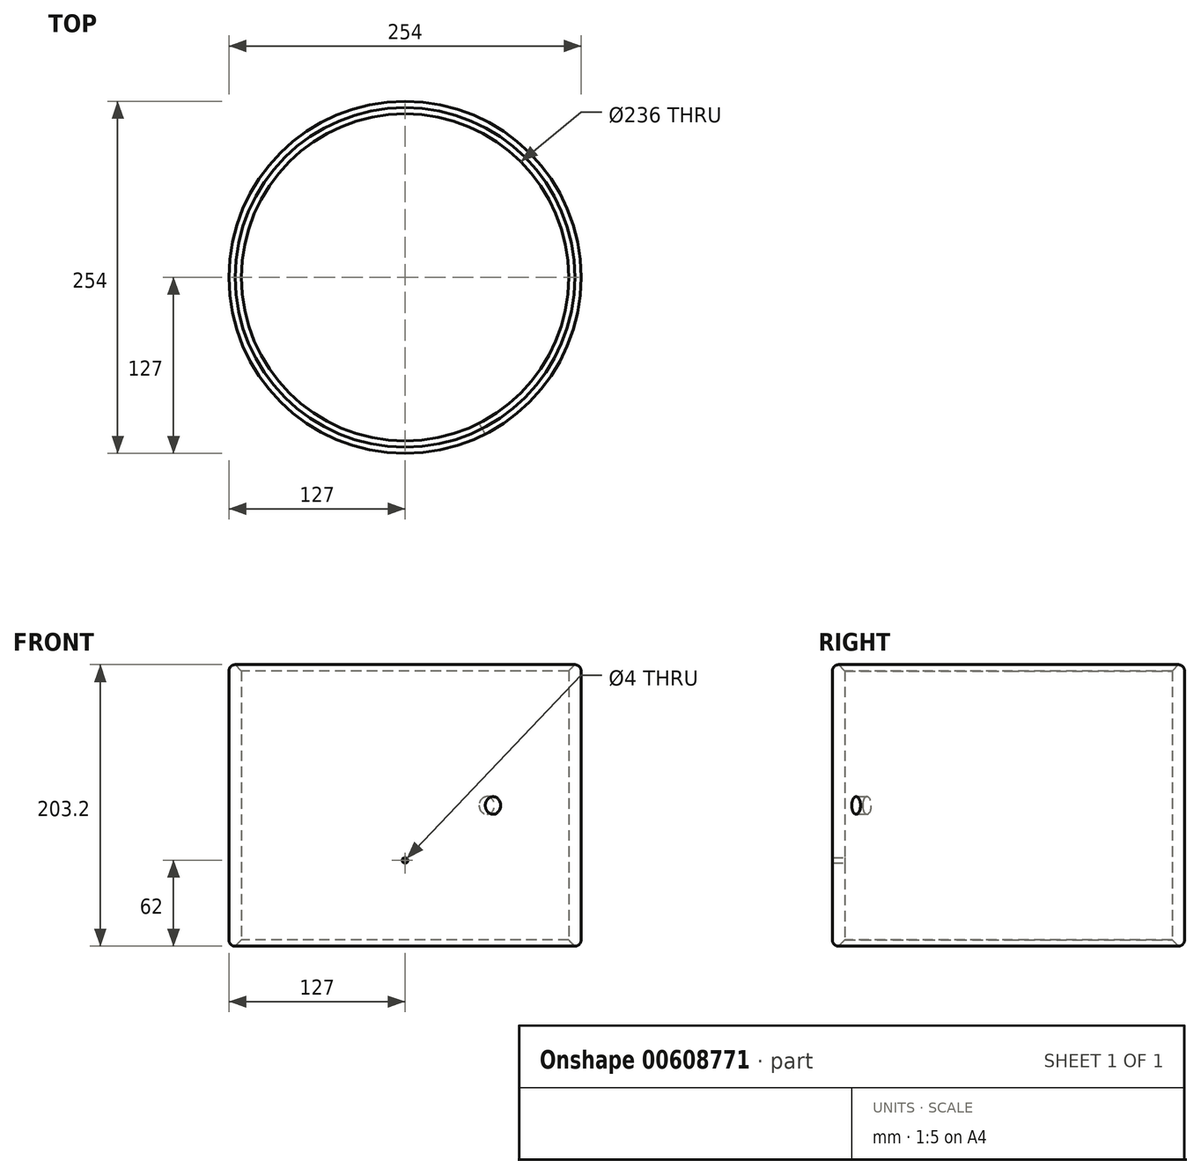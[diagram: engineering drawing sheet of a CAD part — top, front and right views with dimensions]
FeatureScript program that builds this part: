
annotation { "Feature Type Name" : "Feature", "Feature Type Description" : "" }
export const myFeature = defineFeature(function(context is Context, id is Id, definition is map)
    precondition{}
    {
        {
            var Q0;
            Q0=qCreatedBy(makeId("Top.planeOp"),FACE);
            var sketch = newSketch(context, id + "F0", { "sketchPlane" : qUnion([Q0])});
            skCircle(sketch, "E0", {"center": v(0, 0) * mm, "radius": 127 * mm});
            skCircle(sketch, "E1.0", {"center": v(0, 0) * mm, "radius": 118 * mm});
            skCircle(sketch, "E2.0", {"center": v(0, 0) * mm, "radius": 122.5 * mm});
            skLineSegment(sketch, "E3", {"start": v(0, 0) * mm, "end": v(0, 54.17) * mm, "construction": true});
            skSolve(sketch);
        }
        {
            var Q0;
            Q0=makeQuery(id+"F0.imprint","IMPRINT",FACE,{"disambiguationData":[TD([[makeQuery(id+"F0.imprint","IMPRINT",EDGE,{"derivedFrom":sQuery(id+"F0.wireOp",EDGE,"E0")}),1.0]])]});
            var Q1;
            Q1=makeQuery(id+"F0.imprint","IMPRINT",FACE,{"disambiguationData":[TD([[makeQuery(id+"F0.imprint","IMPRINT",EDGE,{"derivedFrom":sQuery(id+"F0.wireOp",EDGE,"E1.0")}),-1.0]])]});
            extrude(context, id + "F1", {"entities" : qUnion([Q0, Q1]), "depth" : 203.2 * mm, "offsetDistance" : 25 * mm});
        }
        {
            var Q0;
            Q0=makeQuery(id+"F1.opExtrude","CAP_EDGE",EDGE,{"disambiguationData":[OSD([sQuery(id+"F0.wireOp",EDGE,"E1.0")])],"isStart":false});
            chamfer(context, id + "F2", {"entities" : qUnion([Q0]), "width" : 4.5 * mm, "tangentPropagation" : true});
        }
        {
            var Q0;
            Q0=makeQuery(id+"F1.opExtrude","CAP_EDGE",EDGE,{"disambiguationData":[OSD([sQuery(id+"F0.wireOp",EDGE,"E0")])],"isStart":false});
            fillet(context, id + "F3", {"entities" : qUnion([Q0]), "radius" : 4.5 * mm, "tangentPropagation" : true, "allowEdgeOverflow" : false});
        }
        {
            var Q0;
            Q0=makeQuery(id+"F1.opExtrude","CAP_EDGE",EDGE,{"disambiguationData":[OSD([sQuery(id+"F0.wireOp",EDGE,"E1.0")])],"isStart":true});
            chamfer(context, id + "F4", {"entities" : qUnion([Q0]), "width" : 4.5 * mm, "tangentPropagation" : true});
        }
        {
            var Q0;
            Q0=makeQuery(id+"F1.opExtrude","CAP_EDGE",EDGE,{"disambiguationData":[OSD([sQuery(id+"F0.wireOp",EDGE,"E0")])],"isStart":true});
            fillet(context, id + "F5", {"entities" : qUnion([Q0]), "radius" : 4.5 * mm, "tangentPropagation" : true, "allowEdgeOverflow" : false});
        }
        {
            var Q0;
            Q0=sQuery(id+"F0.wireOp",EDGE,"E3");
            var Q1;
            Q1=sQuery(id+"F0.wireOp",VERTEX,"E3.start");
            cPlane(context, id + "F6", {"entities" : qUnion([Q0, Q1]), "cplaneType" : CPlaneType.LINE_POINT, "offset" : 25 * mm, "width" : 150 * mm, "height" : 150 * mm});
        }
        {
            var Q0;
            Q0=qCreatedBy(id+"F6.planeOp",FACE);
            var sketch = newSketch(context, id + "F7", { "sketchPlane" : qUnion([Q0])});
            skCircle(sketch, "E4", {"center": v(0, 101.6) * mm, "radius": 2 * mm});
            skLineSegment(sketch, "E5", {"start": v(0, 0) * mm, "end": v(0, 62) * mm, "construction": true});
            skCircle(sketch, "E6", {"center": v(0, 62) * mm, "radius": 2 * mm});
            skLineSegment(sketch, "E7", {"start": v(0, 101.6) * mm, "end": v(-27.1, 101.6) * mm, "construction": true});
            skCircle(sketch, "E8.MirrorC", {"center": v(0, 141.2) * mm, "radius": 2 * mm});
            skLineSegment(sketch, "E9", {"start": v(0, 141.2) * mm, "end": v(0, 203.2) * mm, "construction": true});
            skSolve(sketch);
        }
        {
            var Q0;
            Q0=makeQuery(id+"F7.imprint","IMPRINT",FACE,{"disambiguationData":[TD([[makeQuery(id+"F7.imprint","IMPRINT",EDGE,{"derivedFrom":sQuery(id+"F7.wireOp",EDGE,"E8.MirrorC")}),-1.0]])]});
            var Q1;
            Q1=makeQuery(id+"F7.imprint","IMPRINT",FACE,{"disambiguationData":[TD([[makeQuery(id+"F7.imprint","IMPRINT",EDGE,{"derivedFrom":sQuery(id+"F7.wireOp",EDGE,"E6")}),1.0]])]});
            extrude(context, id + "F8", {"entities" : qUnion([Q0, Q1]), "operationType" : NewBodyOperationType.REMOVE, "oppositeDirection" : true, "depth" : 234 * mm, "offsetDistance" : 25 * mm});
        }
        {
            var Q0;
            Q0=sQuery(id+"F7.wireOp",EDGE,"E9");
            var Q1;
            Q1=qCreatedBy(id+"F6.planeOp",FACE);
            cPlane(context, id + "F9", {"entities" : qUnion([Q0, Q1]), "cplaneType" : CPlaneType.LINE_ANGLE, "offset" : 25 * mm, "angle" : 30 * degree, "width" : 150 * mm, "height" : 150 * mm});
        }
        {
            var Q0;
            Q0=qCreatedBy(id+"F9.planeOp",FACE);
            var sketch = newSketch(context, id + "F10", { "sketchPlane" : qUnion([Q0])});
            skPoint(sketch, "E10", {"position": v(0, 101.6) * mm});
            skCircle(sketch, "E11", {"center": v(0, 101.6) * mm, "radius": 6.35 * mm});
            skSolve(sketch);
        }
        {
            var Q0;
            Q0 = qSketchRegion(id + "F10", true);
            extrude(context, id + "F11", {"entities" : qUnion([Q0]), "operationType" : NewBodyOperationType.REMOVE, "depth" : 231 * mm, "offsetDistance" : 25 * mm});
        }
    });
